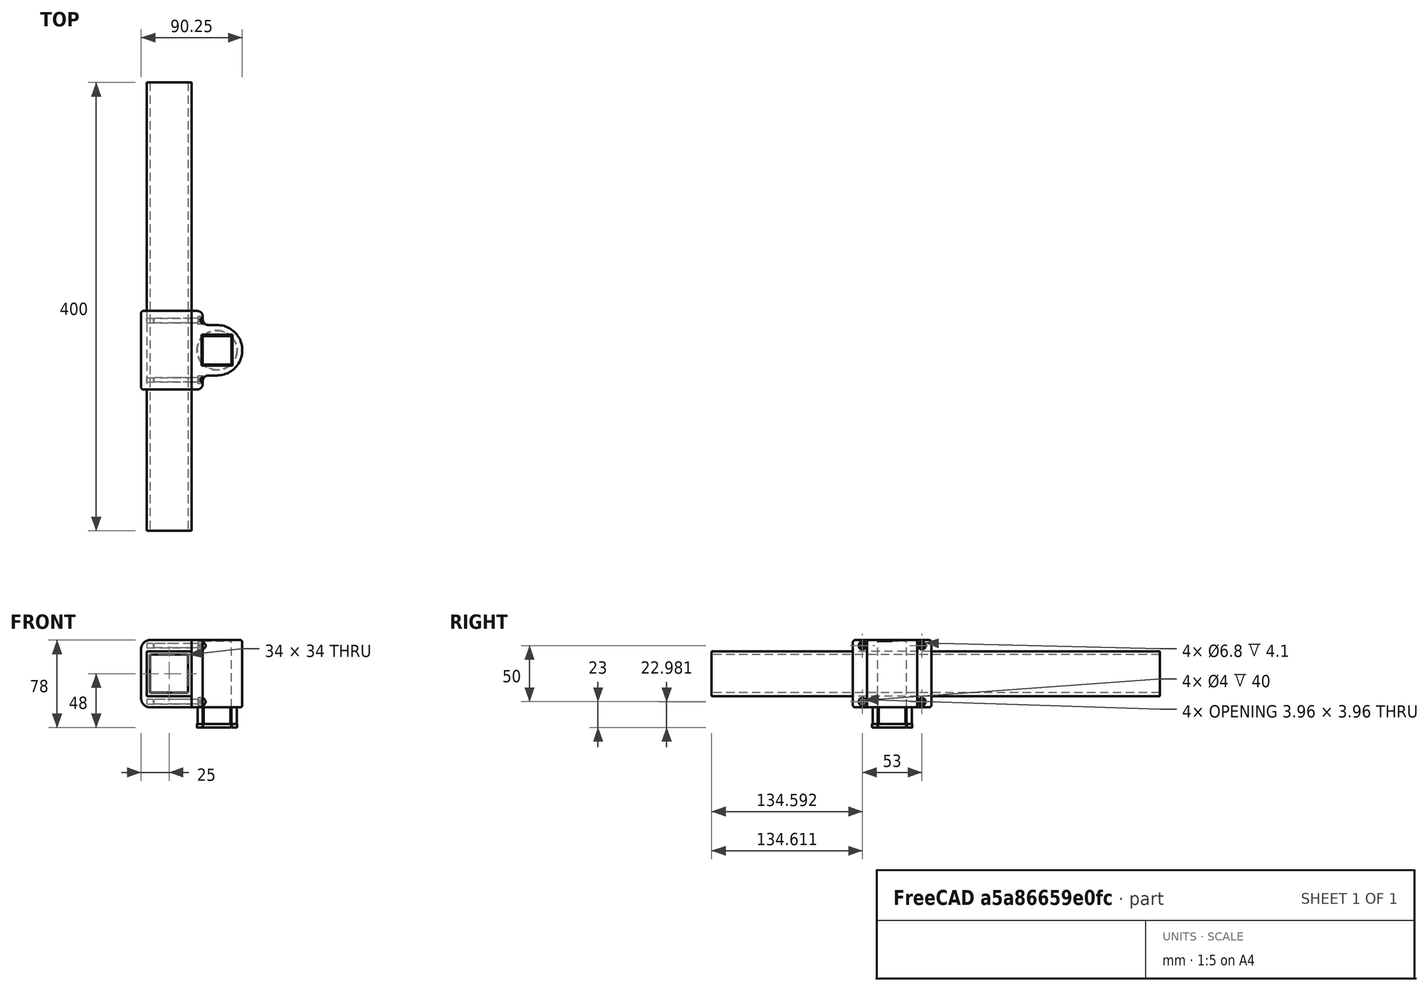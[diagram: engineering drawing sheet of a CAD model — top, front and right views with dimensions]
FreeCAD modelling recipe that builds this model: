
FCSTD DOCUMENT  (FreeCAD 0.20R29603 (Git))
Label: BG_DaichselStütze 2.0
License: All rights reserved
LicenseURL: http://en.wikipedia.org/wiki/All_rights_reserved
objects: App::FeaturePython×20, Part::FeaturePython×7
note: 7 computed .brp shape members not serialized (recipe doc carries the construction recipe); baked Part::Feature solids carry a one-line shape summary decoded from their .brp

FEATURE [Part::FeaturePython] b_DeichselRohr_001_  label="DeichselRohr_001"  # a2plus imported part (geometry in sourceFile) (typed FeaturePython)
  Placement = pos=(0,11,0) rot=(0,0,1;0rad)
  a2p_Version = 0.4.60n
  fixedPosition = true
  objectType = a2pPart
  sourceFile = ./../DeichselRohr/DeichselRohr.FCStd
  subassemblyImport = false
  timeLastImport = 1.69101e+09
  updateColors = true
FEATURE [Part::FeaturePython] b_DeichselSchelle_2_0_001_  label="DeichselSchelle 2.0_001"  # a2plus imported part (geometry in sourceFile) (typed FeaturePython)
  Placement = pos=(20,-192.889,1.11766e-08) rot=(0,0,1;0rad)
  a2p_Version = 0.4.60n
  fixedPosition = false
  objectType = a2pPart
  sourceFile = ./../DaichselSchelle 2.0/DeichselSchelle 2.0.FCStd
  subassemblyImport = false
  timeLastImport = 1.69119e+09
  updateColors = true
FEATURE [Part::FeaturePython] b_Deichselst_xc3_xbctze_2_0_St_xc3_xbctzenklemme_001_  label="Deichselstütze 2.0 Stützenklemme_001"  # a2plus imported part (geometry in sourceFile) (typed FeaturePython)
  Placement = pos=(42.75,-227.889,-30) rot=(0,0,1;0rad)
  a2p_Version = 0.4.60n
  fixedPosition = false
  objectType = a2pPart
  sourceFile = ./../Deichselstütze 2.0 Stützenklemme/Deichselstütze 2.0 Stützenklemme.FCStd
  subassemblyImport = false
  timeLastImport = 1.69119e+09
  updateColors = true
FEATURE [Part::FeaturePython] Screw  label="M4x40-Screw"  # Fasteners workbench fastener (typed FeaturePython)
  Placement = pos=(25.9,-254.389,25) rot=(0,1,0;1.5708rad)
  diameter = 5
  invert = false
  leftHanded = false
  length = 10
  lengthCustom = 40
  matchOuter = false
  offset = 0
  thread = false
  type = 45
FEATURE [Part::FeaturePython] Screw001  label="M4x40-Screw011"  # Fasteners workbench fastener (typed FeaturePython)
  Placement = pos=(25.9,-201.389,25) rot=(-0.545713,0.63592,-0.545713;2.00877rad)
  diameter = 5
  invert = false
  leftHanded = false
  length = 10
  lengthCustom = 40
  matchOuter = false
  offset = 0
  thread = false
  type = 45
FEATURE [Part::FeaturePython] Screw002  label="M4x40-Screw014"  # Fasteners workbench fastener (typed FeaturePython)
  Placement = pos=(25.9,-254.389,-25) rot=(0.579547,-0.572931,0.579547;4.18215rad)
  diameter = 5
  invert = false
  leftHanded = false
  length = 10
  lengthCustom = 40
  matchOuter = false
  offset = 0
  thread = false
  type = 45
FEATURE [Part::FeaturePython] Screw003  label="M4x40-Screw013"  # Fasteners workbench fastener (typed FeaturePython)
  Placement = pos=(25.9,-201.389,-25) rot=(-0.684336,-0.251731,-0.684336;3.63481rad)
  diameter = 5
  invert = false
  leftHanded = false
  length = 10
  lengthCustom = 40
  matchOuter = false
  offset = 0
  thread = false
  type = 45
FEATURE [App::FeaturePython] axisCoincident_001  label="axisCoincident_001__DeichselSchelle 2.0_001"  # a2plus constraint (typed FeaturePython)
  Object1 = b_DeichselRohr_001_
  Object2 = b_DeichselSchelle_2_0_001_
  ParentTreeObject = -> b_DeichselRohr_001_
  SubElement1 = Edge8
  SubElement2 = Edge16
  Suppressed = false
  Type = axial
  directionConstraint = 0
  lockRotation = false
FEATURE [App::FeaturePython] axisCoincident_001_mirror  label="axisCoincident_001__DeichselRohr_001"  # a2plus constraint (typed FeaturePython)
  Object1 = b_DeichselRohr_001_
  Object2 = b_DeichselSchelle_2_0_001_
  ParentTreeObject = -> b_DeichselSchelle_2_0_001_
  SubElement1 = Edge8
  SubElement2 = Edge16
  Suppressed = false
  Type = axial
  directionConstraint = 0
  lockRotation = false
FEATURE [App::FeaturePython] axisCoincident_002  label="axisCoincident_002__DeichselSchelle 2.0_001"  # a2plus constraint (typed FeaturePython)
  Object1 = Screw
  Object2 = b_DeichselSchelle_2_0_001_
  ParentTreeObject = -> Screw
  SubElement1 = Face17
  SubElement2 = Face12
  Suppressed = false
  Type = axial
  directionConstraint = 1
  lockRotation = false
FEATURE [App::FeaturePython] axisCoincident_002_mirror  label="axisCoincident_002__M4x40-Screw"  # a2plus constraint (typed FeaturePython)
  Object1 = Screw
  Object2 = b_DeichselSchelle_2_0_001_
  ParentTreeObject = -> b_DeichselSchelle_2_0_001_
  SubElement1 = Face17
  SubElement2 = Face12
  Suppressed = false
  Type = axial
  directionConstraint = 1
  lockRotation = false
FEATURE [App::FeaturePython] axisCoincident_003  label="axisCoincident_003__DeichselSchelle 2.0_001"  # a2plus constraint (typed FeaturePython)
  Object1 = Screw001
  Object2 = b_DeichselSchelle_2_0_001_
  ParentTreeObject = -> Screw001
  SubElement1 = Face17
  SubElement2 = Face13
  Suppressed = false
  Type = axial
  directionConstraint = 1
  lockRotation = false
FEATURE [App::FeaturePython] axisCoincident_003_mirror  label="axisCoincident_003__M4x40-Screw001"  # a2plus constraint (typed FeaturePython)
  Object1 = Screw001
  Object2 = b_DeichselSchelle_2_0_001_
  ParentTreeObject = -> b_DeichselSchelle_2_0_001_
  SubElement1 = Face17
  SubElement2 = Face13
  Suppressed = false
  Type = axial
  directionConstraint = 1
  lockRotation = false
FEATURE [App::FeaturePython] axisCoincident_004  label="axisCoincident_004__DeichselSchelle 2.0_001"  # a2plus constraint (typed FeaturePython)
  Object1 = Screw002
  Object2 = b_DeichselSchelle_2_0_001_
  ParentTreeObject = -> Screw002
  SubElement1 = Face17
  SubElement2 = Face27
  Suppressed = false
  Type = axial
  directionConstraint = 1
  lockRotation = false
FEATURE [App::FeaturePython] axisCoincident_004_mirror  label="axisCoincident_004__M4x40-Screw002"  # a2plus constraint (typed FeaturePython)
  Object1 = Screw002
  Object2 = b_DeichselSchelle_2_0_001_
  ParentTreeObject = -> b_DeichselSchelle_2_0_001_
  SubElement1 = Face17
  SubElement2 = Face27
  Suppressed = false
  Type = axial
  directionConstraint = 1
  lockRotation = false
FEATURE [App::FeaturePython] axisCoincident_005  label="axisCoincident_005__DeichselSchelle 2.0_001"  # a2plus constraint (typed FeaturePython)
  Object1 = Screw003
  Object2 = b_DeichselSchelle_2_0_001_
  ParentTreeObject = -> Screw003
  SubElement1 = Face17
  SubElement2 = Face28
  Suppressed = false
  Type = axial
  directionConstraint = 1
  lockRotation = false
FEATURE [App::FeaturePython] axisCoincident_005_mirror  label="axisCoincident_005__M4x40-Screw003"  # a2plus constraint (typed FeaturePython)
  Object1 = Screw003
  Object2 = b_DeichselSchelle_2_0_001_
  ParentTreeObject = -> b_DeichselSchelle_2_0_001_
  SubElement1 = Face17
  SubElement2 = Face28
  Suppressed = false
  Type = axial
  directionConstraint = 1
  lockRotation = false
FEATURE [App::FeaturePython] planeCoincident_001  label="planeCoincident_001__Deichselstütze 2.0 Stützenklemme_001"  # a2plus constraint (typed FeaturePython)
  Object1 = Screw
  Object2 = b_Deichselst_xc3_xbctze_2_0_St_xc3_xbctzenklemme_001_
  ParentTreeObject = -> Screw
  SubElement1 = Face13
  SubElement2 = Face82
  Suppressed = false
  Type = plane
  directionConstraint = 0
  offset = 0
FEATURE [App::FeaturePython] planeCoincident_001_mirror  label="planeCoincident_001__M4x40-Screw"  # a2plus constraint (typed FeaturePython)
  Object1 = Screw
  Object2 = b_Deichselst_xc3_xbctze_2_0_St_xc3_xbctzenklemme_001_
  ParentTreeObject = -> b_Deichselst_xc3_xbctze_2_0_St_xc3_xbctzenklemme_001_
  SubElement1 = Face13
  SubElement2 = Face82
  Suppressed = false
  Type = plane
  directionConstraint = 0
  offset = 0
FEATURE [App::FeaturePython] planeCoincident_002  label="planeCoincident_002__DeichselSchelle 2.0_001"  # a2plus constraint (typed FeaturePython)
  Object1 = b_Deichselst_xc3_xbctze_2_0_St_xc3_xbctzenklemme_001_
  Object2 = b_DeichselSchelle_2_0_001_
  ParentTreeObject = -> b_Deichselst_xc3_xbctze_2_0_St_xc3_xbctzenklemme_001_
  SubElement1 = Face6
  SubElement2 = Face5
  Suppressed = false
  Type = plane
  directionConstraint = 1
  offset = 0
FEATURE [App::FeaturePython] planeCoincident_002_mirror  label="planeCoincident_002__Deichselstütze 2.0 Stützenklemme_001"  # a2plus constraint (typed FeaturePython)
  Object1 = b_Deichselst_xc3_xbctze_2_0_St_xc3_xbctzenklemme_001_
  Object2 = b_DeichselSchelle_2_0_001_
  ParentTreeObject = -> b_DeichselSchelle_2_0_001_
  SubElement1 = Face6
  SubElement2 = Face5
  Suppressed = false
  Type = plane
  directionConstraint = 1
  offset = 0
FEATURE [App::FeaturePython] planeCoincident_003  label="planeCoincident_003__Deichselstütze 2.0 Stützenklemme_001"  # a2plus constraint (typed FeaturePython)
  Object1 = Screw002
  Object2 = b_Deichselst_xc3_xbctze_2_0_St_xc3_xbctzenklemme_001_
  ParentTreeObject = -> Screw002
  SubElement1 = Face13
  SubElement2 = Face80
  Suppressed = false
  Type = plane
  directionConstraint = 0
  offset = 0
FEATURE [App::FeaturePython] planeCoincident_003_mirror  label="planeCoincident_003__M4x40-Screw014"  # a2plus constraint (typed FeaturePython)
  Object1 = Screw002
  Object2 = b_Deichselst_xc3_xbctze_2_0_St_xc3_xbctzenklemme_001_
  ParentTreeObject = -> b_Deichselst_xc3_xbctze_2_0_St_xc3_xbctzenklemme_001_
  SubElement1 = Face13
  SubElement2 = Face80
  Suppressed = false
  Type = plane
  directionConstraint = 0
  offset = 0
FEATURE [App::FeaturePython] planeCoincident_004  label="planeCoincident_004__M4x40-Screw011"  # a2plus constraint (typed FeaturePython)
  Object1 = b_Deichselst_xc3_xbctze_2_0_St_xc3_xbctzenklemme_001_
  Object2 = Screw001
  ParentTreeObject = -> b_Deichselst_xc3_xbctze_2_0_St_xc3_xbctzenklemme_001_
  SubElement1 = Face81
  SubElement2 = Face13
  Suppressed = false
  Type = plane
  directionConstraint = 0
  offset = 0
FEATURE [App::FeaturePython] planeCoincident_004_mirror  label="planeCoincident_004__Deichselstütze 2.0 Stützenklemme_001"  # a2plus constraint (typed FeaturePython)
  Object1 = b_Deichselst_xc3_xbctze_2_0_St_xc3_xbctzenklemme_001_
  Object2 = Screw001
  ParentTreeObject = -> Screw001
  SubElement1 = Face81
  SubElement2 = Face13
  Suppressed = false
  Type = plane
  directionConstraint = 0
  offset = 0
FEATURE [App::FeaturePython] planeCoincident_005  label="planeCoincident_005__Deichselstütze 2.0 Stützenklemme_001"  # a2plus constraint (typed FeaturePython)
  Object1 = Screw003
  Object2 = b_Deichselst_xc3_xbctze_2_0_St_xc3_xbctzenklemme_001_
  ParentTreeObject = -> Screw003
  SubElement1 = Face13
  SubElement2 = Face79
  Suppressed = false
  Type = plane
  directionConstraint = 0
  offset = 0
FEATURE [App::FeaturePython] planeCoincident_005_mirror  label="planeCoincident_005__M4x40-Screw013"  # a2plus constraint (typed FeaturePython)
  Object1 = Screw003
  Object2 = b_Deichselst_xc3_xbctze_2_0_St_xc3_xbctzenklemme_001_
  ParentTreeObject = -> b_Deichselst_xc3_xbctze_2_0_St_xc3_xbctzenklemme_001_
  SubElement1 = Face13
  SubElement2 = Face79
  Suppressed = false
  Type = plane
  directionConstraint = 0
  offset = 0
